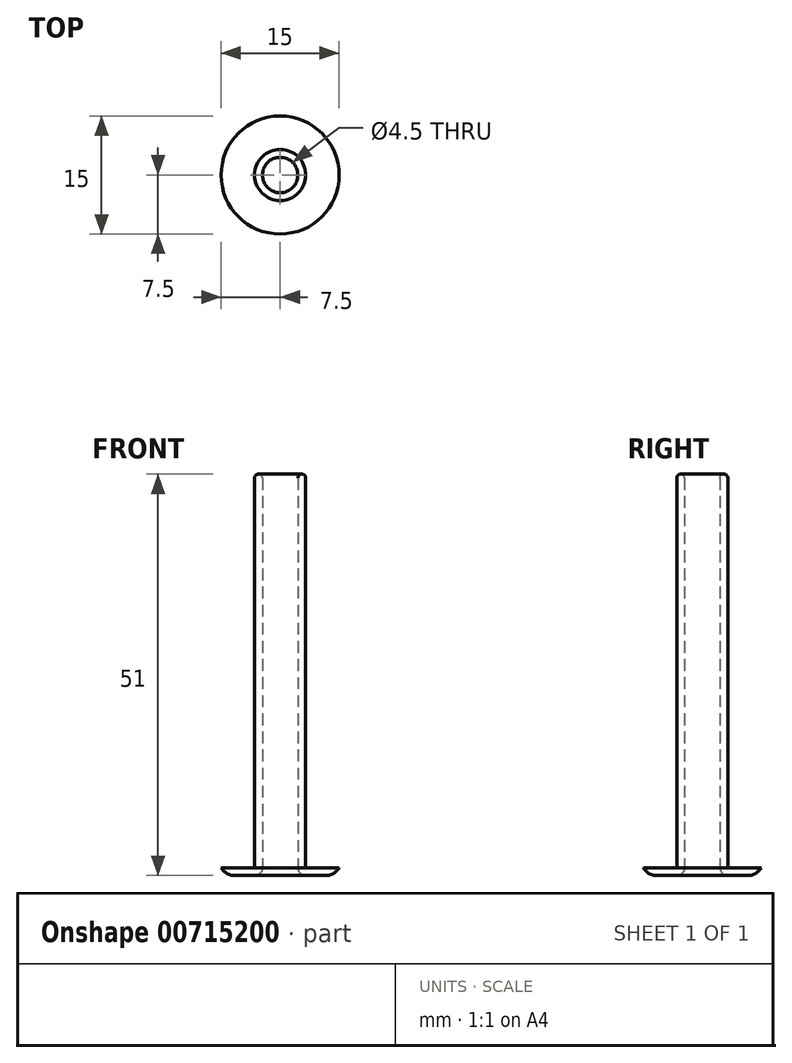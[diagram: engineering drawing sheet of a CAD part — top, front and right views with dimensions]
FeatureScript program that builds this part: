
annotation { "Feature Type Name" : "Feature", "Feature Type Description" : "" }
export const myFeature = defineFeature(function(context is Context, id is Id, definition is map)
    precondition{}
    {
        {
            var Q0;
            Q0=qCreatedBy(makeId("Top.planeOp"),FACE);
            var sketch = newSketch(context, id + "F0", { "sketchPlane" : qUnion([Q0])});
            skCircle(sketch, "E0", {"center": v(0, 0) * mm, "radius": 7.5 * mm});
            skCircle(sketch, "E1", {"center": v(0, 0) * mm, "radius": 3.25 * mm});
            skCircle(sketch, "E2", {"center": v(0, 0) * mm, "radius": 2.25 * mm});
            skSolve(sketch);
        }
        {
            var Q0;
            Q0=makeQuery(id+"F0.imprint","IMPRINT",FACE,{"disambiguationData":[TD([[makeQuery(id+"F0.imprint","IMPRINT",EDGE,{"derivedFrom":sQuery(id+"F0.wireOp",EDGE,"E1")}),1.0]])]});
            extrude(context, id + "F1", {"entities" : qUnion([Q0]), "depth" : 51 * mm, "offsetDistance" : 25 * mm});
        }
        {
            var Q0;
            Q0=makeQuery(id+"F0.imprint","IMPRINT",FACE,{"disambiguationData":[TD([[makeQuery(id+"F0.imprint","IMPRINT",EDGE,{"derivedFrom":sQuery(id+"F0.wireOp",EDGE,"E0")}),1.0]])]});
            extrude(context, id + "F2", {"entities" : qUnion([Q0]), "operationType" : NewBodyOperationType.ADD, "depth" : 1 * mm, "offsetDistance" : 25 * mm});
        }
        {
            var Q0;
            Q0=makeQuery(id+"F1.opExtrude","CAP_EDGE",EDGE,{"disambiguationData":[OSD([sQuery(id+"F0.wireOp",EDGE,"E1")])],"isStart":false});
            var Q1;
            Q1=makeQuery(id+"F1.opExtrude","CAP_EDGE",EDGE,{"disambiguationData":[OSD([sQuery(id+"F0.wireOp",EDGE,"E2")])],"isStart":false});
            fillet(context, id + "F3", {"entities" : qUnion([Q0, Q1]), "radius" : 0.5 * mm, "tangentPropagation" : true, "allowEdgeOverflow" : false});
        }
        {
            var Q0;
            Q0=makeQuery(id+"F2.opExtrude","CAP_EDGE",EDGE,{"disambiguationData":[OSD([sQuery(id+"F0.wireOp",EDGE,"E0")])],"isStart":true});
            fillet(context, id + "F4", {"entities" : qUnion([Q0]), "radius" : 2 * mm, "tangentPropagation" : true, "allowEdgeOverflow" : false});
        }
        {
            var Q0;
            Q0=makeQuery(id+"F1.opExtrude","CAP_EDGE",EDGE,{"disambiguationData":[OSD([sQuery(id+"F0.wireOp",EDGE,"E2")])],"isStart":true});
            fillet(context, id + "F5", {"entities" : qUnion([Q0]), "radius" : 1 * mm, "tangentPropagation" : true, "allowEdgeOverflow" : false});
        }
    });
